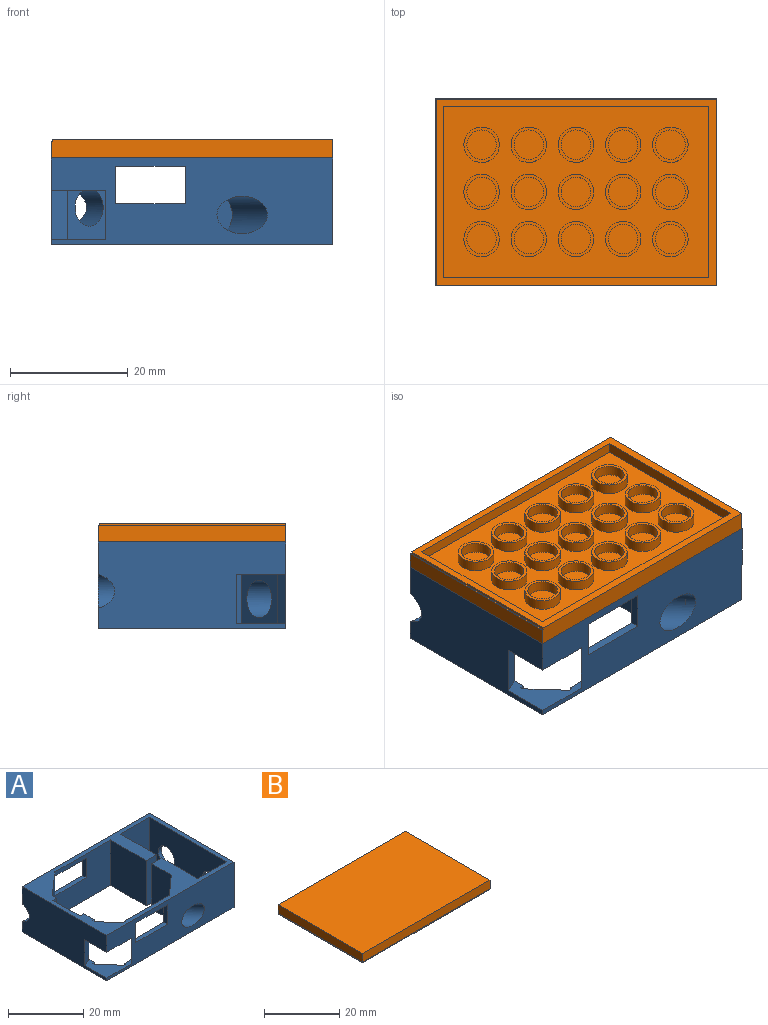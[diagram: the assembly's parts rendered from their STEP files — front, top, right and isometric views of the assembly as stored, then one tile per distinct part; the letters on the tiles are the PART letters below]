
ASSEMBLY  parts=2 mates=1
PART A: 50 faces, bbox 49.2x39x14.7 mm
  f0: plane 14.73x13.48mm, normal (-1,0,0), area 198.6mm2, adj f2,f3,f7,f10
  f1: plane 11.81x1.4mm, normal (0,0,-1), area 16.5mm2, adj f10,f11,f32,f34
  f2: plane 47.8x31.8mm, normal (0,0,1), area 399.7mm2, adj f0,f3,f4,f5,f6,f8,f9,f10
  f3: plane 14.73x3.81mm, normal (0,-1,0), area 56.1mm2, adj f0,f2,f7,f44
  f4: plane 14.73x3.81mm, normal (0,1,0), area 56.1mm2, adj f2,f7,f15,f46
  f5: plane 31.8x14.73mm, normal (-1,0,0), area 387.6mm2, adj f2,f7,f9,f11,f20,f22,f23,f41
  f6: plane 14.73x4.05mm, normal (1,0,0), area 41.4mm2, adj f2,f7,f22,f23,f26,f31,f39,f41
  f7: plane 47.8x31.8mm, normal (0,0,-1), area 399.7mm2, adj f0,f3,f4,f5,f6,f8,f9,f10
  f8: plane 16.95x14.73mm, normal (0,1,0), area 150.7mm2, adj f2,f7,f14,f17,f21,f22,f23,f24
  f9: plane 47.8x14.73mm, normal (0,-1,0), area 508.7mm2, adj f2,f5,f7,f14,f19,f21,f22,f23
  f10: plane 20.85x14.73mm, normal (0,-1,0), area 232.1mm2, adj f0,f1,f2,f7,f18,f33,f34
  f11: plane 47.8x14.73mm, normal (0,1,0), area 597.1mm2, adj f1,f2,f5,f7,f20,f32,f33,f34
  f12: plane 14.73x1.69mm, normal (1,0,0), area 24.9mm2, adj f2,f7,f18,f38
  f13: plane 5.84x5.25mm, normal (0.74,0.67,0), area 7mm2, adj f7,f22,f28,f30
  f14: plane 11.81x1.4mm, normal (0,0,-1), area 16.5mm2, adj f8,f9,f36,f37
  f15: plane 14.73x7.31mm, normal (-1,0,0), area 107.7mm2, adj f2,f4,f7,f17
  f16: plane 5.84x5.46mm, normal (0.74,0.67,0), area 42.9mm2, adj f2,f23,f25,f27
  f17: plane 14.73x6.86mm, normal (-0.67,0.74,0), area 104.3mm2, adj f2,f7,f8,f15,f19
  f18: plane 14.73x8.16mm, normal (0.66,-0.75,0), area 127.9mm2, adj f2,f7,f10,f12,f20,f32
  f19: cylinder r=3.17mm len=10.89mm, axis (-0.67,0.74,0), area 120.4mm2, adj f9,f17
  f20: cylinder r=3.17mm len=10.4mm, axis (0.66,-0.75,0), area 124.1mm2, adj f5,f11,f18
  f21: plane 8.38x1.56mm, normal (-0.67,0.74,0), area 17.5mm2, adj f8,f9,f22,f23
  f22: plane 10.84x9.54mm, normal (0,0,1), area 44.2mm2, adj f5,f6,f8,f9,f13,f21,f28,f29
  f23: plane 10.84x9.54mm, normal (0,0,-1), area 44.2mm2, adj f5,f6,f8,f9,f16,f21,f24,f25
  f24: plane 5.46x0.38mm, normal (-1,0,0), area 2.1mm2, adj f2,f8,f23,f25
  f25: plane 5.46x0.59mm, normal (0,1,0), area 3.2mm2, adj f2,f16,f23,f24
  f26: plane 5.46x0.66mm, normal (0,-1,0), area 3.6mm2, adj f2,f6,f23,f27
  f27: plane 5.46x0.51mm, normal (1,0,0), area 2.8mm2, adj f2,f16,f23,f26
  f28: plane 0.89x0.59mm, normal (0,1,0), area 0.5mm2, adj f7,f13,f22,f29
  f29: plane 0.89x0.38mm, normal (-1,0,0), area 0.3mm2, adj f7,f8,f22,f28
  f30: plane 0.89x0.51mm, normal (1,0,0), area 0.5mm2, adj f7,f13,f22,f31
  f31: plane 0.89x0.66mm, normal (0,-1,0), area 0.6mm2, adj f6,f7,f22,f30
  f32: plane 6.35x1.4mm, normal (1,0,0), area 8.9mm2, adj f1,f11,f18,f33
  f33: plane 11.81x1.4mm, normal (0,0,1), area 16.5mm2, adj f10,f11,f32,f34
  f34: plane 6.35x1.4mm, normal (-1,0,0), area 8.9mm2, adj f1,f10,f11,f33
  f35: plane 11.81x1.4mm, normal (0,0,1), area 16.5mm2, adj f8,f9,f36,f37
  f36: plane 6.35x1.4mm, normal (-1,0,0), area 8.9mm2, adj f8,f9,f14,f35
  f37: plane 6.35x1.4mm, normal (1,0,0), area 8.9mm2, adj f8,f9,f14,f35
  f38: plane 14.73x1.4mm, normal (0,-1,0), area 20.6mm2, adj f2,f7,f12,f40
  f39: plane 14.73x1.4mm, normal (0,1,0), area 20.6mm2, adj f2,f6,f7,f40
  f40: plane 14.73x10.16mm, normal (1,0,0), area 149.7mm2, adj f2,f7,f38,f39
  f41: plane 8.38x2.8mm, normal (0.41,-0.91,0), area 25.7mm2, adj f5,f6,f22,f23
  f42: plane 31.8x14.73mm, normal (1,0,0), area 409.6mm2, adj f2,f7,f9,f11,f48,f49
  f43: plane 29.01x14.73mm, normal (-1,0,0), area 368.4mm2, adj f2,f7,f45,f47,f48,f49
  f44: plane 14.73x13.49mm, normal (1,0,0), area 198.7mm2, adj f2,f3,f7,f45
  f45: plane 14.73x10.92mm, normal (0,-1,0), area 160.9mm2, adj f2,f7,f43,f44
  f46: plane 14.73x13.49mm, normal (1,0,0), area 198.7mm2, adj f2,f4,f7,f47
  f47: plane 14.73x10.92mm, normal (0,1,0), area 160.9mm2, adj f2,f7,f43,f46
  f48: cylinder r=3.06mm len=6.12mm, axis (1,0,0), area 24.4mm2, adj f42,f43
  f49: cylinder r=3.06mm len=6.12mm, axis (1,0,0), area 24.4mm2, adj f42,f43
PART B: 74 faces, bbox 47.8x31.8x3.2 mm
  f0: plane 47.6x31.6mm, normal (0,0,-1), area 199.2mm2, adj f1,f4,f6,f7,f8,f9,f71,f72
  f1: plane 47.8x3.2mm, normal (0,1,0), area 152.9mm2, adj f0,f2,f4,f5,f71,f73
  f2: plane 31.8x2.8mm, normal (-1,0,0), area 89mm2, adj f1,f3,f5,f73
  f3: plane 47.8x2.8mm, normal (0,-1,0), area 133.8mm2, adj f2,f4,f5,f73
  f4: plane 31.8x3.2mm, normal (1,0,0), area 101.7mm2, adj f0,f1,f3,f5,f72,f73
  f5: plane 47.8x31.8mm, normal (0,0,1), area 1520mm2, adj f1,f2,f3,f4
  f6: plane 45x1.8mm, normal (0,-1,0), area 81mm2, adj f0,f7,f9,f10
  f7: plane 29x1.8mm, normal (1,0,0), area 52.2mm2, adj f0,f6,f8,f10
  f8: plane 45x1.8mm, normal (0,1,0), area 81mm2, adj f0,f7,f9,f10
  f9: plane 29x1.8mm, normal (-1,0,0), area 52.2mm2, adj f0,f6,f8,f10
  f10: plane 45x29mm, normal (0,0,-1), area 880.9mm2, adj f6,f7,f8,f9,f12,f16,f20,f24
  f11: cylinder r=2.5mm len=5mm, axis (0,0,1), area 28.3mm2, adj f13,f14
  f12: cylinder r=3mm len=6mm, axis (0,0,1), area 33.9mm2, adj f10,f13
  f13: plane 6x6mm, normal (0,0,-1), area 8.6mm2, adj f11,f12
  f14: plane 5x5mm, normal (0,0,-1), area 19.6mm2, adj f11
  f15: cylinder r=2.5mm len=5mm, axis (0,0,1), area 28.3mm2, adj f17,f18
  f16: cylinder r=3mm len=6mm, axis (0,0,1), area 33.9mm2, adj f10,f17
  f17: plane 6x6mm, normal (0,0,-1), area 8.6mm2, adj f15,f16
  f18: plane 5x5mm, normal (0,0,-1), area 19.6mm2, adj f15
  f19: cylinder r=2.5mm len=5mm, axis (0,0,1), area 28.3mm2, adj f21,f22
  f20: cylinder r=3mm len=6mm, axis (0,0,1), area 33.9mm2, adj f10,f21
  f21: plane 6x6mm, normal (0,0,-1), area 8.6mm2, adj f19,f20
  f22: plane 5x5mm, normal (0,0,-1), area 19.6mm2, adj f19
  f23: cylinder r=2.5mm len=5mm, axis (0,0,1), area 28.3mm2, adj f25,f26
  f24: cylinder r=3mm len=6mm, axis (0,0,1), area 33.9mm2, adj f10,f25
  f25: plane 6x6mm, normal (0,0,-1), area 8.6mm2, adj f23,f24
  f26: plane 5x5mm, normal (0,0,-1), area 19.6mm2, adj f23
  f27: cylinder r=2.5mm len=5mm, axis (0,0,1), area 28.3mm2, adj f29,f30
  f28: cylinder r=3mm len=6mm, axis (0,0,1), area 33.9mm2, adj f10,f29
  f29: plane 6x6mm, normal (0,0,-1), area 8.6mm2, adj f27,f28
  f30: plane 5x5mm, normal (0,0,-1), area 19.6mm2, adj f27
  f31: cylinder r=2.5mm len=5mm, axis (0,0,1), area 28.3mm2, adj f33,f34
  f32: cylinder r=3mm len=6mm, axis (0,0,1), area 33.9mm2, adj f10,f33
  f33: plane 6x6mm, normal (0,0,-1), area 8.6mm2, adj f31,f32
  f34: plane 5x5mm, normal (0,0,-1), area 19.6mm2, adj f31
  f35: cylinder r=2.5mm len=5mm, axis (0,0,1), area 28.3mm2, adj f37,f38
  f36: cylinder r=3mm len=6mm, axis (0,0,1), area 33.9mm2, adj f10,f37
  f37: plane 6x6mm, normal (0,0,-1), area 8.6mm2, adj f35,f36
  f38: plane 5x5mm, normal (0,0,-1), area 19.6mm2, adj f35
  f39: cylinder r=2.5mm len=5mm, axis (0,0,1), area 28.3mm2, adj f41,f42
  f40: cylinder r=3mm len=6mm, axis (0,0,1), area 33.9mm2, adj f10,f41
  f41: plane 6x6mm, normal (0,0,-1), area 8.6mm2, adj f39,f40
  f42: plane 5x5mm, normal (0,0,-1), area 19.6mm2, adj f39
  f43: cylinder r=2.5mm len=5mm, axis (0,0,1), area 28.3mm2, adj f45,f46
  f44: cylinder r=3mm len=6mm, axis (0,0,1), area 33.9mm2, adj f10,f45
  f45: plane 6x6mm, normal (0,0,-1), area 8.6mm2, adj f43,f44
  f46: plane 5x5mm, normal (0,0,-1), area 19.6mm2, adj f43
  f47: cylinder r=2.5mm len=5mm, axis (0,0,1), area 28.3mm2, adj f49,f50
  f48: cylinder r=3mm len=6mm, axis (0,0,1), area 33.9mm2, adj f10,f49
  f49: plane 6x6mm, normal (0,0,-1), area 8.6mm2, adj f47,f48
  f50: plane 5x5mm, normal (0,0,-1), area 19.6mm2, adj f47
  f51: cylinder r=2.5mm len=5mm, axis (0,0,1), area 28.3mm2, adj f53,f54
  f52: cylinder r=3mm len=6mm, axis (0,0,1), area 33.9mm2, adj f10,f53
  f53: plane 6x6mm, normal (0,0,-1), area 8.6mm2, adj f51,f52
  f54: plane 5x5mm, normal (0,0,-1), area 19.6mm2, adj f51
  f55: cylinder r=2.5mm len=5mm, axis (0,0,1), area 28.3mm2, adj f57,f58
  f56: cylinder r=3mm len=6mm, axis (0,0,1), area 33.9mm2, adj f10,f57
  f57: plane 6x6mm, normal (0,0,-1), area 8.6mm2, adj f55,f56
  f58: plane 5x5mm, normal (0,0,-1), area 19.6mm2, adj f55
  f59: cylinder r=2.5mm len=5mm, axis (0,0,1), area 28.3mm2, adj f61,f62
  f60: cylinder r=3mm len=6mm, axis (0,0,1), area 33.9mm2, adj f10,f61
  f61: plane 6x6mm, normal (0,0,-1), area 8.6mm2, adj f59,f60
  f62: plane 5x5mm, normal (0,0,-1), area 19.6mm2, adj f59
  f63: cylinder r=2.5mm len=5mm, axis (0,0,1), area 28.3mm2, adj f65,f66
  f64: cylinder r=3mm len=6mm, axis (0,0,1), area 33.9mm2, adj f10,f65
  f65: plane 6x6mm, normal (0,0,-1), area 8.6mm2, adj f63,f64
  f66: plane 5x5mm, normal (0,0,-1), area 19.6mm2, adj f63
  f67: cylinder r=2.5mm len=5mm, axis (0,0,1), area 28.3mm2, adj f69,f70
  f68: cylinder r=3mm len=6mm, axis (0,0,1), area 33.9mm2, adj f10,f69
  f69: plane 6x6mm, normal (0,0,-1), area 8.6mm2, adj f67,f68
  f70: plane 5x5mm, normal (0,0,-1), area 19.6mm2, adj f67
  f71: plane 31.6x0.4mm, normal (-1,0,0), area 12.6mm2, adj f0,f1,f72,f73
  f72: plane 47.6x0.4mm, normal (0,-1,0), area 19mm2, adj f0,f4,f71,f73
  f73: plane 47.8x31.8mm, normal (0,0,-1), area 15.9mm2, adj f1,f2,f3,f4,f71,f72
PLACE A t=(-30.01,21.77,-34.65)mm
PLACE B rot(axis=(-1,0,0),180deg) t=(-31.41,53.57,-21.85)mm
MATE planar A.f2 <-> B.f39  axis (0,0,1) through (-8.13,37.57,-25.05)mm
